# Revit family: QSK Правый 260_320_360
name_source: partatom
category: Оборудование
revit_build: Autodesk Revit 2017 (Build: 20171027_0315(x64)
units: mm (PartAtom-declared; Revit-internal decimal feet)

## family parameters
Всегда вертикально = Да
На основе рабочей плоскости = Нет
Общий = Нет
При загрузке вырезать с полостями = Нет
Размер круглого соединителя = Использовать диаметр
Тип детали = Нормальный
Точка расчета площади = Нет

## types (3) — shared parameters
ADSK_Версия Revit = 2017
ADSK_Версия семейства = v1
ADSK_Завод-изготовитель = Moehlenhoff
ADSK_Количество = 1
D = 15 мм
D_подкл = 35 мм
ID01 = Стандартное
ID02 = Сбоку сторона окна
ID03 = Сбоку сторона помещения
RF_1l = 40 мм
RF_2l = 62 мм
RR_1l = 40 мм
RR_2l = 62 мм
t03 = t03
t04 = t04_l
t05 = t05_l
t07 = t07
tcode = tcode_l
Высота КН = 110 мм
Изготовитель = Moehlenhoff
Корпус = <По категории>
Разработчик = ООО ПРОРУБИМ
Разработчик (URL) = http://prorubim.com
Разработчик (телефон) = +7(495)649-85-43
Решетка толщина = 15 мм

## per-type parameters (varying)
| type | LA | RA | RF_1h | RF_2h | RR_1h | RR_2h | RS_1h | RS_1l | RS_2h | RS_2l | Решетка ширина | Ширина КВ |
| QSK EC-260x110h | 210 мм | 226 мм | 38 мм | 62 мм | 38 мм | 62 мм | 40 мм | 55 мм | 61 мм | 100 мм | 254 мм | 260 мм |
| QSK EC-320x110h | 180 мм | 196 мм | 50 мм | 62 мм | 50 мм | 62 мм | 51 мм | 109 мм | 40 мм | 55 мм | 314 мм | 320 мм |
| QSK EC-360x110h | 210 мм | 226 мм | 38 мм | 60 мм | 38 мм | 60 мм | 38 мм | 52 мм | 60 мм | 200 мм | 354 мм | 360 мм |
